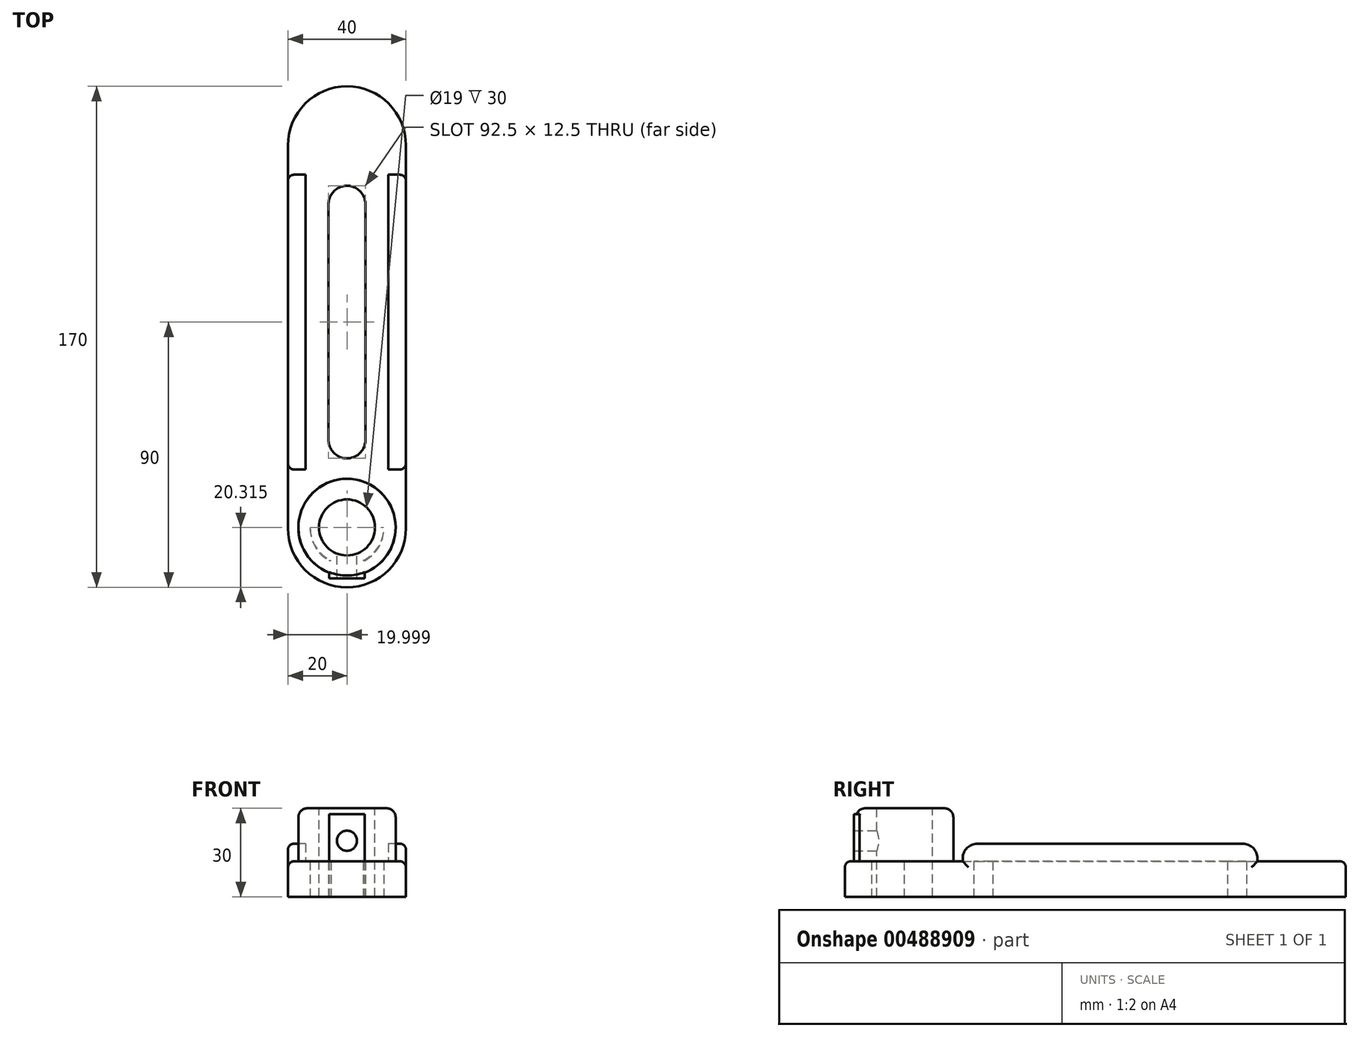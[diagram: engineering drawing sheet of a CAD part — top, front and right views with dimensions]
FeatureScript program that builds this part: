
annotation { "Feature Type Name" : "Feature", "Feature Type Description" : "" }
export const myFeature = defineFeature(function(context is Context, id is Id, definition is map)
    precondition{}
    {
        {
            var Q0;
            Q0=qCreatedBy(makeId("Top.planeOp"),FACE);
            var sketch = newSketch(context, id + "F0", { "sketchPlane" : qUnion([Q0])});
            skLineSegment(sketch, "E0.top", {"start": v(20, 80) * mm, "end": v(-20, 80) * mm});
            skLineSegment(sketch, "E0.left", {"start": v(20, -70) * mm, "end": v(20, 80) * mm});
            skLineSegment(sketch, "E0.right", {"start": v(-20, -70) * mm, "end": v(-20, 80) * mm});
            skPoint(sketch, "E0.middle", {"position": v(0, 0) * mm});
            skLineSegment(sketch, "E1", {"start": v(0, 0) * mm, "end": v(0, 40) * mm, "construction": true});
            skLineSegment(sketch, "E2", {"start": v(0, 40) * mm, "end": v(0, -40) * mm, "construction": true});
            skArc(sketch, "E3", {"start": v(-6.25, -40) * mm, "mid": v(0.07, -46.25) * mm, "end": v(6.25, -39.85) * mm});
            skArc(sketch, "E4", {"start": v(6.25, 39.85) * mm, "mid": v(0.07, 46.25) * mm, "end": v(-6.25, 40) * mm});
            skLineSegment(sketch, "E5", {"start": v(-6.25, 40) * mm, "end": v(-6.25, -40) * mm});
            skLineSegment(sketch, "E6", {"start": v(6.25, 40.15) * mm, "end": v(6.25, -40.15) * mm});
            skLineSegment(sketch, "E7", {"start": v(0, -90) * mm, "end": v(0, -70) * mm, "construction": true});
            skLineSegment(sketch, "E8", {"start": v(0, -70) * mm, "end": v(62.72, -70) * mm, "construction": true});
            skCircle(sketch, "E9", {"center": v(0, -70) * mm, "radius": 12.5 * mm});
            skArc(sketch, "E10", {"start": v(-20, -70) * mm, "mid": v(0, -90) * mm, "end": v(20, -70) * mm});
            skSolve(sketch);
        }
        {
            var Q0;
            Q0=makeQuery(id+"F0.imprint","IMPRINT",FACE,{"disambiguationData":[TD([[makeQuery(id+"F0.imprint","IMPRINT",EDGE,{"derivedFrom":sQuery(id+"F0.wireOp",EDGE,"E0.top")}),1.0]])]});
            extrude(context, id + "F1", {"entities" : qUnion([Q0]), "depth" : 12 * mm});
        }
        {
            var Q0;
            Q0=qCreatedBy(makeId("Top.planeOp"),FACE);
            var sketch = newSketch(context, id + "F2", { "sketchPlane" : qUnion([Q0])});
            skCircle(sketch, "E11", {"center": v(0, -69.69) * mm, "radius": 12.5 * mm});
            skCircle(sketch, "E12", {"center": v(0, -69.69) * mm, "radius": 16.5 * mm});
            skCircle(sketch, "E13", {"center": v(0, -69.69) * mm, "radius": 9.5 * mm});
            skSolve(sketch);
        }
        {
            var Q0;
            Q0=makeQuery(id+"F2.imprint","IMPRINT",FACE,{"disambiguationData":[TD([[makeQuery(id+"F2.imprint","IMPRINT",EDGE,{"derivedFrom":sQuery(id+"F2.wireOp",EDGE,"E11")}),-1.0]])]});
            var Q1;
            Q1=makeQuery(id+"F2.imprint","IMPRINT",FACE,{"disambiguationData":[TD([[makeQuery(id+"F2.imprint","IMPRINT",EDGE,{"derivedFrom":sQuery(id+"F2.wireOp",EDGE,"E11")}),1.0]])]});
            extrude(context, id + "F3", {"entities" : qUnion([Q0, Q1]), "operationType" : NewBodyOperationType.ADD, "depth" : 30 * mm, "hasSecondDirection" : true, "secondDirectionOppositeDirection" : false, "secondDirectionDepth" : 12 * mm});
        }
        {
            var Q0;
            Q0=makeQuery(id+"F2.imprint","IMPRINT",FACE,{"disambiguationData":[TD([[makeQuery(id+"F2.imprint","IMPRINT",EDGE,{"derivedFrom":sQuery(id+"F2.wireOp",EDGE,"E13")}),1.0]])]});
            var Q1;
            Q1=makeQuery(id+"F2.imprint","IMPRINT",FACE,{"disambiguationData":[TD([[makeQuery(id+"F2.imprint","IMPRINT",EDGE,{"derivedFrom":sQuery(id+"F2.wireOp",EDGE,"E11")}),1.0]])]});
            extrude(context, id + "F4", {"entities" : qUnion([Q0, Q1]), "operationType" : NewBodyOperationType.ADD, "depth" : 30 * mm});
        }
        {
            var Q0;
            Q0=qCreatedBy(makeId("Top.planeOp"),FACE);
            var sketch = newSketch(context, id + "F5", { "sketchPlane" : qUnion([Q0])});
            skCircle(sketch, "E14", {"center": v(0, -69.69) * mm, "radius": 9.5 * mm});
            skSolve(sketch);
        }
        {
            var Q0;
            Q0 = qSketchRegion(id + "F5", true);
            extrude(context, id + "F6", {"entities" : qUnion([Q0]), "operationType" : NewBodyOperationType.REMOVE, "oppositeDirection" : true, "depth" : 25 * mm, "hasSecondDirection" : true, "secondDirectionOppositeDirection" : false, "secondDirectionDepth" : 100 * mm});
        }
        {
            var Q0;
            Q0=makeQuery(id+"F3.opExtrude","CAP_EDGE",EDGE,{"disambiguationData":[OSD([sQuery(id+"F2.wireOp",EDGE,"E12")])],"isStart":false});
            var Q1;
            Q1=makeQuery(id+"F3.opExtrude","CAP_EDGE",EDGE,{"disambiguationData":[OSD([sQuery(id+"F2.wireOp",EDGE,"E12")])],"isStart":true});
            fillet(context, id + "F7", {"entities" : qUnion([Q0, Q1]), "radius" : 3 * mm, "tangentPropagation" : true, "allowEdgeOverflow" : false});
        }
        {
            var Q0;
            Q0=qCreatedBy(makeId("Front.planeOp"),FACE);
            var sketch = newSketch(context, id + "F8", { "sketchPlane" : qUnion([Q0])});
            skLineSegment(sketch, "E15", {"start": v(14, 0) * mm, "end": v(20, 0) * mm, "construction": true});
            skLineSegment(sketch, "E16", {"start": v(20, 0) * mm, "end": v(20, 18) * mm});
            skLineSegment(sketch, "E17", {"start": v(20, 18) * mm, "end": v(14, 18) * mm});
            skLineSegment(sketch, "E18", {"start": v(14, 18) * mm, "end": v(14, 12) * mm});
            skLineSegment(sketch, "E19", {"start": v(-14, 12) * mm, "end": v(-14, 18) * mm});
            skLineSegment(sketch, "E20", {"start": v(-14, 18) * mm, "end": v(-20, 18) * mm});
            skLineSegment(sketch, "E21", {"start": v(-20, 18) * mm, "end": v(-20, 0) * mm});
            skLineSegment(sketch, "E22", {"start": v(-20, 0) * mm, "end": v(-14, 0) * mm});
            skLineSegment(sketch, "E23", {"start": v(-14, 12) * mm, "end": v(-14, 0) * mm});
            skLineSegment(sketch, "E24", {"start": v(14, 12) * mm, "end": v(14, 0) * mm});
            skLineSegment(sketch, "E25.trimOffspring", {"start": v(0, 0) * mm, "end": v(20, 0) * mm});
            skSolve(sketch);
        }
        {
            var Q0;
            Q0 = qSketchRegion(id + "F8", true);
            extrude(context, id + "F9", {"entities" : qUnion([Q0]), "operationType" : NewBodyOperationType.ADD, "depth" : 50 * mm, "hasSecondDirection" : true, "secondDirectionOppositeDirection" : true, "secondDirectionDepth" : 50 * mm});
        }
        {
            var Q0;
            Q0=makeQuery(id+"F9.opExtrude","CAP_EDGE",EDGE,{"disambiguationData":[OSD([sQuery(id+"F8.wireOp",EDGE,"E17")])],"isStart":true});
            var Q1;
            Q1=makeQuery(id+"F9.opExtrude","CAP_EDGE",EDGE,{"disambiguationData":[OSD([sQuery(id+"F8.wireOp",EDGE,"E20")])],"isStart":true});
            var Q2;
            Q2=makeQuery(id+"F9.opExtrude","CAP_EDGE",EDGE,{"disambiguationData":[OSD([sQuery(id+"F8.wireOp",EDGE,"E20")])],"isStart":false});
            var Q3;
            Q3=makeQuery(id+"F9.opExtrude","CAP_EDGE",EDGE,{"disambiguationData":[OSD([sQuery(id+"F8.wireOp",EDGE,"E17")])],"isStart":false});
            fillet(context, id + "F10", {"entities" : qUnion([Q0, Q1, Q2, Q3]), "radius" : 5 * mm, "tangentPropagation" : true, "allowEdgeOverflow" : false});
        }
        {
            var Q0;
            Q0=makeQuery(id+"F1.opExtrude","SWEPT_EDGE",EDGE,{"disambiguationData":[OSD([sQuery(id+"F0.wireOp",EDGE,"E0.top"),sQuery(id+"F0.wireOp",EDGE,"E0.right")])]});
            var Q1;
            Q1=makeQuery(id+"F1.opExtrude","SWEPT_EDGE",EDGE,{"disambiguationData":[OSD([sQuery(id+"F0.wireOp",EDGE,"E0.top"),sQuery(id+"F0.wireOp",EDGE,"E0.left")])]});
            fillet(context, id + "F11", {"entities" : qUnion([Q0, Q1]), "radius" : 20 * mm, "tangentPropagation" : true, "allowEdgeOverflow" : false});
        }
        {
            var Q0;
            Q0=qCreatedBy(makeId("Top.planeOp"),FACE);
            var sketch = newSketch(context, id + "F12", { "sketchPlane" : qUnion([Q0])});
            skLineSegment(sketch, "E26.bottom", {"start": v(6, -86.93) * mm, "end": v(-6, -86.93) * mm});
            skLineSegment(sketch, "E26.top", {"start": v(6, -80.93) * mm, "end": v(-6, -80.93) * mm});
            skLineSegment(sketch, "E26.left", {"start": v(6, -86.93) * mm, "end": v(6, -80.93) * mm});
            skLineSegment(sketch, "E26.right", {"start": v(-6, -86.93) * mm, "end": v(-6, -80.93) * mm});
            skPoint(sketch, "E26.middle", {"position": v(0, -83.93) * mm});
            skSolve(sketch);
        }
        {
            var Q0;
            Q0 = qSketchRegion(id + "F12", true);
            extrude(context, id + "F13", {"entities" : qUnion([Q0]), "operationType" : NewBodyOperationType.ADD, "depth" : 28 * mm});
        }
        {
            var Q0;
            Q0=qCreatedBy(makeId("Front.planeOp"),FACE);
            var sketch = newSketch(context, id + "F14", { "sketchPlane" : qUnion([Q0])});
            skLineSegment(sketch, "E27", {"start": v(0, 0) * mm, "end": v(0, 19) * mm, "construction": true});
            skLineSegment(sketch, "E28", {"start": v(0, 19) * mm, "end": v(-52.5, 19) * mm, "construction": true});
            skCircle(sketch, "E29", {"center": v(0, 19) * mm, "radius": 3.4 * mm});
            skSolve(sketch);
        }
        {
            var Q0;
            Q0 = qSketchRegion(id + "F14", true);
            extrude(context, id + "F15", {"entities" : qUnion([Q0]), "operationType" : NewBodyOperationType.REMOVE, "depth" : 100 * mm, "hasSecondDirection" : true, "secondDirectionOppositeDirection" : false, "secondDirectionDepth" : 70 * mm});
        }
        {
            var Q0;
            {var subQ1=sQuery(id+"F0.wireOp",EDGE,"E0.left");var subQ2=sQuery(id+"F0.wireOp",EDGE,"E0.top");Q0=makeQuery(id+"F9.boolean.opBoolean","SPLIT",EDGE,{"disambiguationData":[TD([makeQuery(id+"F1.opExtrude","SWEPT_FACE",FACE,{"disambiguationData":[OSD([subQ2])]})])],"derivedFrom":makeQuery(id+"F1.opExtrude","CAP_EDGE",EDGE,{"disambiguationData":[OSD([subQ1])],"isStart":false})});}
            var Q1;
            {var subQ0=sQuery(id+"F0.wireOp",EDGE,"E0.right");var subQ1=sQuery(id+"F0.wireOp",EDGE,"E0.top");Q1=makeQuery(id+"F11.opFillet","BLEND_EDGE",EDGE,{"blendedFrom":[makeQuery(id+"F1.opExtrude","SWEPT_EDGE",EDGE,{"disambiguationData":[OSD([subQ1,subQ0])]}),makeQuery(id+"F1.opExtrude","CAP_FACE",FACE,{"disambiguationData":[OSD([subQ1,sQuery(id+"F0.wireOp",EDGE,"E0.left"),subQ0,sQuery(id+"F0.wireOp",EDGE,"E3"),sQuery(id+"F0.wireOp",EDGE,"E4"),sQuery(id+"F0.wireOp",EDGE,"E5"),sQuery(id+"F0.wireOp",EDGE,"E6"),sQuery(id+"F0.wireOp",EDGE,"E9"),sQuery(id+"F0.wireOp",EDGE,"E10")])],"isStart":false})],"blendedInto":[makeQuery(id+"F1.opExtrude","CAP_FACE",FACE,{"disambiguationData":[OSD([subQ1,sQuery(id+"F0.wireOp",EDGE,"E0.left"),subQ0,sQuery(id+"F0.wireOp",EDGE,"E3"),sQuery(id+"F0.wireOp",EDGE,"E4"),sQuery(id+"F0.wireOp",EDGE,"E5"),sQuery(id+"F0.wireOp",EDGE,"E6"),sQuery(id+"F0.wireOp",EDGE,"E9"),sQuery(id+"F0.wireOp",EDGE,"E10")])],"isStart":false})]});}
            var Q2;
            {var subQ1=sQuery(id+"F0.wireOp",EDGE,"E0.right");var subQ2=sQuery(id+"F0.wireOp",EDGE,"E0.top");Q2=makeQuery(id+"F9.boolean.opBoolean","SPLIT",EDGE,{"disambiguationData":[TD([makeQuery(id+"F1.opExtrude","SWEPT_FACE",FACE,{"disambiguationData":[OSD([subQ2])]})])],"derivedFrom":makeQuery(id+"F1.opExtrude","CAP_EDGE",EDGE,{"disambiguationData":[OSD([subQ1])],"isStart":false})});}
            var Q3;
            {var subQ1=sQuery(id+"F0.wireOp",EDGE,"E10");var subQ2=sQuery(id+"F0.wireOp",EDGE,"E0.left");Q3=makeQuery(id+"F9.boolean.opBoolean","SPLIT",EDGE,{"disambiguationData":[TD([makeQuery(id+"F1.opExtrude","SWEPT_FACE",FACE,{"disambiguationData":[OSD([subQ1])]})])],"derivedFrom":makeQuery(id+"F1.opExtrude","CAP_EDGE",EDGE,{"disambiguationData":[OSD([subQ2])],"isStart":false})});}
            var Q4;
            Q4=makeQuery(id+"F10.opFillet","BLEND_EDGE",EDGE,{"blendedFrom":[makeQuery(id+"F9.opExtrude","CAP_EDGE",EDGE,{"disambiguationData":[OSD([sQuery(id+"F8.wireOp",EDGE,"E20")])],"isStart":false}),makeQuery(id+"F9.boolean.opBoolean","MERGE",FACE,{"derivedFrom":[makeQuery(id+"F1.opExtrude","SWEPT_FACE",FACE,{"disambiguationData":[OSD([sQuery(id+"F0.wireOp",EDGE,"E0.right")])]}),makeQuery(id+"F9.opExtrude","SWEPT_FACE",FACE,{"disambiguationData":[OSD([sQuery(id+"F8.wireOp",EDGE,"E21")])]})]})],"blendedInto":[makeQuery(id+"F9.boolean.opBoolean","MERGE",FACE,{"derivedFrom":[makeQuery(id+"F1.opExtrude","SWEPT_FACE",FACE,{"disambiguationData":[OSD([sQuery(id+"F0.wireOp",EDGE,"E0.right")])]}),makeQuery(id+"F9.opExtrude","SWEPT_FACE",FACE,{"disambiguationData":[OSD([sQuery(id+"F8.wireOp",EDGE,"E21")])]})]})]});
            var Q5;
            Q5=makeQuery(id+"F9.opExtrude","SWEPT_EDGE",EDGE,{"disambiguationData":[OSD([sQuery(id+"F8.wireOp",EDGE,"E20"),sQuery(id+"F8.wireOp",EDGE,"E21")])]});
            var Q6;
            Q6=makeQuery(id+"F9.opExtrude","SWEPT_EDGE",EDGE,{"disambiguationData":[OSD([sQuery(id+"F8.wireOp",EDGE,"E16"),sQuery(id+"F8.wireOp",EDGE,"E17")])]});
            var Q7;
            Q7=makeQuery(id+"F10.opFillet","BLEND_EDGE",EDGE,{"blendedFrom":[makeQuery(id+"F9.opExtrude","CAP_EDGE",EDGE,{"disambiguationData":[OSD([sQuery(id+"F8.wireOp",EDGE,"E17")])],"isStart":false}),makeQuery(id+"F9.boolean.opBoolean","MERGE",FACE,{"derivedFrom":[makeQuery(id+"F1.opExtrude","SWEPT_FACE",FACE,{"disambiguationData":[OSD([sQuery(id+"F0.wireOp",EDGE,"E0.left")])]}),makeQuery(id+"F9.opExtrude","SWEPT_FACE",FACE,{"disambiguationData":[OSD([sQuery(id+"F8.wireOp",EDGE,"E16")])]})]})],"blendedInto":[makeQuery(id+"F9.boolean.opBoolean","MERGE",FACE,{"derivedFrom":[makeQuery(id+"F1.opExtrude","SWEPT_FACE",FACE,{"disambiguationData":[OSD([sQuery(id+"F0.wireOp",EDGE,"E0.left")])]}),makeQuery(id+"F9.opExtrude","SWEPT_FACE",FACE,{"disambiguationData":[OSD([sQuery(id+"F8.wireOp",EDGE,"E16")])]})]})]});
            fillet(context, id + "F16", {"entities" : qUnion([Q0, Q1, Q2, Q3, Q4, Q5, Q6, Q7]), "radius" : 2 * mm, "tangentPropagation" : true, "allowEdgeOverflow" : false});
        }
    });
